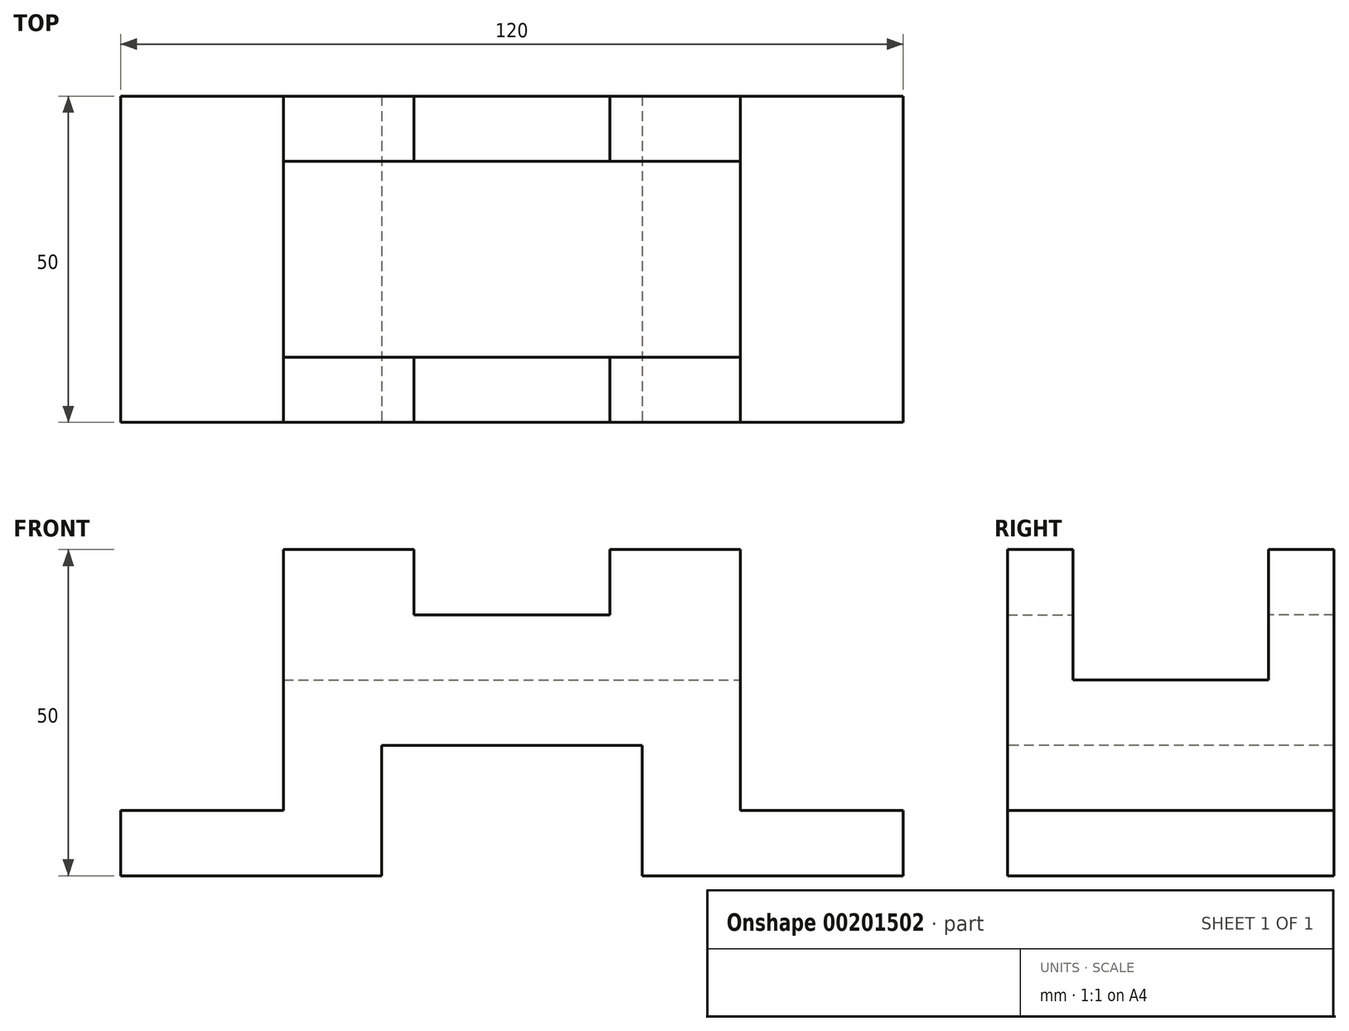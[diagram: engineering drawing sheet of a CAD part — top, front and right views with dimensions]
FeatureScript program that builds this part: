
annotation { "Feature Type Name" : "Feature", "Feature Type Description" : "" }
export const myFeature = defineFeature(function(context is Context, id is Id, definition is map)
    precondition{}
    {
        {
            var Q0;
            Q0=qCreatedBy(makeId("Front.planeOp"),FACE);
            var sketch = newSketch(context, id + "F0", { "sketchPlane" : qUnion([Q0])});
            skLineSegment(sketch, "E0", {"start": v(-60, 0) * mm, "end": v(-20, 0) * mm});
            skLineSegment(sketch, "E1", {"start": v(-20, 0) * mm, "end": v(-20, 20) * mm});
            skLineSegment(sketch, "E2", {"start": v(-20, 20) * mm, "end": v(0, 20) * mm});
            skLineSegment(sketch, "E3", {"start": v(0, 20) * mm, "end": v(0, 40) * mm});
            skLineSegment(sketch, "E4", {"start": v(0, 40) * mm, "end": v(-15, 40) * mm});
            skLineSegment(sketch, "E5", {"start": v(-15, 40) * mm, "end": v(-15, 50) * mm});
            skLineSegment(sketch, "E6", {"start": v(-15, 50) * mm, "end": v(-35, 50) * mm});
            skLineSegment(sketch, "E7", {"start": v(-35, 50) * mm, "end": v(-35, 10) * mm});
            skLineSegment(sketch, "E8", {"start": v(-35, 10) * mm, "end": v(-60, 10) * mm});
            skLineSegment(sketch, "E9", {"start": v(-60, 10) * mm, "end": v(-60, 0) * mm});
            skLineSegment(sketch, "E10", {"start": v(0, 0) * mm, "end": v(0, 20) * mm, "construction": true});
            skLineSegment(sketch, "E11", {"start": v(-35, 30) * mm, "end": v(0, 30) * mm});
            skSolve(sketch);
        }
        {
            var Q0;
            Q0=qSketchRegion(id+"F0",true);
            extrude(context, id + "F1", {"entities" : qUnion([Q0]), "oppositeDirection" : true, "depth" : (50 / 2) * mm});
        }
        {
            var Q0;
            {var subQ1=sQuery(id+"F0.wireOp",EDGE,"E4");Q0=makeQuery(id+"F0.imprint","IMPRINT",FACE,{"disambiguationData":[TD([[makeQuery(id+"F0.imprint","IMPRINT",EDGE,{"derivedFrom":subQ1}),1.0]])]});}
            extrude(context, id + "F2", {"entities" : qUnion([Q0]), "operationType" : NewBodyOperationType.REMOVE, "oppositeDirection" : true, "depth" : (30 / 2) * mm});
        }
        {
            var Q0;
            Q0=makeQuery(id+"F1.opExtrude","SWEPT_BODY",BODY,{"disambiguationData":[OSD([sQuery(id+"F0.wireOp",EDGE,"E0"),sQuery(id+"F0.wireOp",EDGE,"E1"),sQuery(id+"F0.wireOp",EDGE,"E2"),sQuery(id+"F0.wireOp",EDGE,"E3"),sQuery(id+"F0.wireOp",EDGE,"E4"),sQuery(id+"F0.wireOp",EDGE,"E5"),sQuery(id+"F0.wireOp",EDGE,"E6"),sQuery(id+"F0.wireOp",EDGE,"E7"),sQuery(id+"F0.wireOp",EDGE,"E8"),sQuery(id+"F0.wireOp",EDGE,"E9")])]});
            var Q1;
            Q1=makeQuery(id+"F1.opExtrude","SWEPT_FACE",FACE,{"disambiguationData":[OSD([sQuery(id+"F0.wireOp",EDGE,"E3")])]});
            mirror(context, id + "F3", {"operationType" : NewBodyOperationType.ADD, "entities" : qUnion([Q0]), "mirrorPlane" : qUnion([Q1])});
        }
        {
            var Q0;
            Q0=makeQuery(id+"F1.opExtrude","SWEPT_BODY",BODY,{"disambiguationData":[OSD([sQuery(id+"F0.wireOp",EDGE,"E0"),sQuery(id+"F0.wireOp",EDGE,"E1"),sQuery(id+"F0.wireOp",EDGE,"E2"),sQuery(id+"F0.wireOp",EDGE,"E3"),sQuery(id+"F0.wireOp",EDGE,"E4"),sQuery(id+"F0.wireOp",EDGE,"E5"),sQuery(id+"F0.wireOp",EDGE,"E6"),sQuery(id+"F0.wireOp",EDGE,"E7"),sQuery(id+"F0.wireOp",EDGE,"E8"),sQuery(id+"F0.wireOp",EDGE,"E9")])]});
            var Q1;
            Q1=makeQuery(id+"F0.imprint","IMPRINT",FACE,{"disambiguationData":[TD([[makeQuery(id+"F0.imprint","IMPRINT",EDGE,{"derivedFrom":sQuery(id+"F0.wireOp",EDGE,"E0")}),1.0]])]});
            mirror(context, id + "F4", {"operationType" : NewBodyOperationType.ADD, "entities" : qUnion([Q0]), "mirrorPlane" : qUnion([Q1])});
        }
    });
